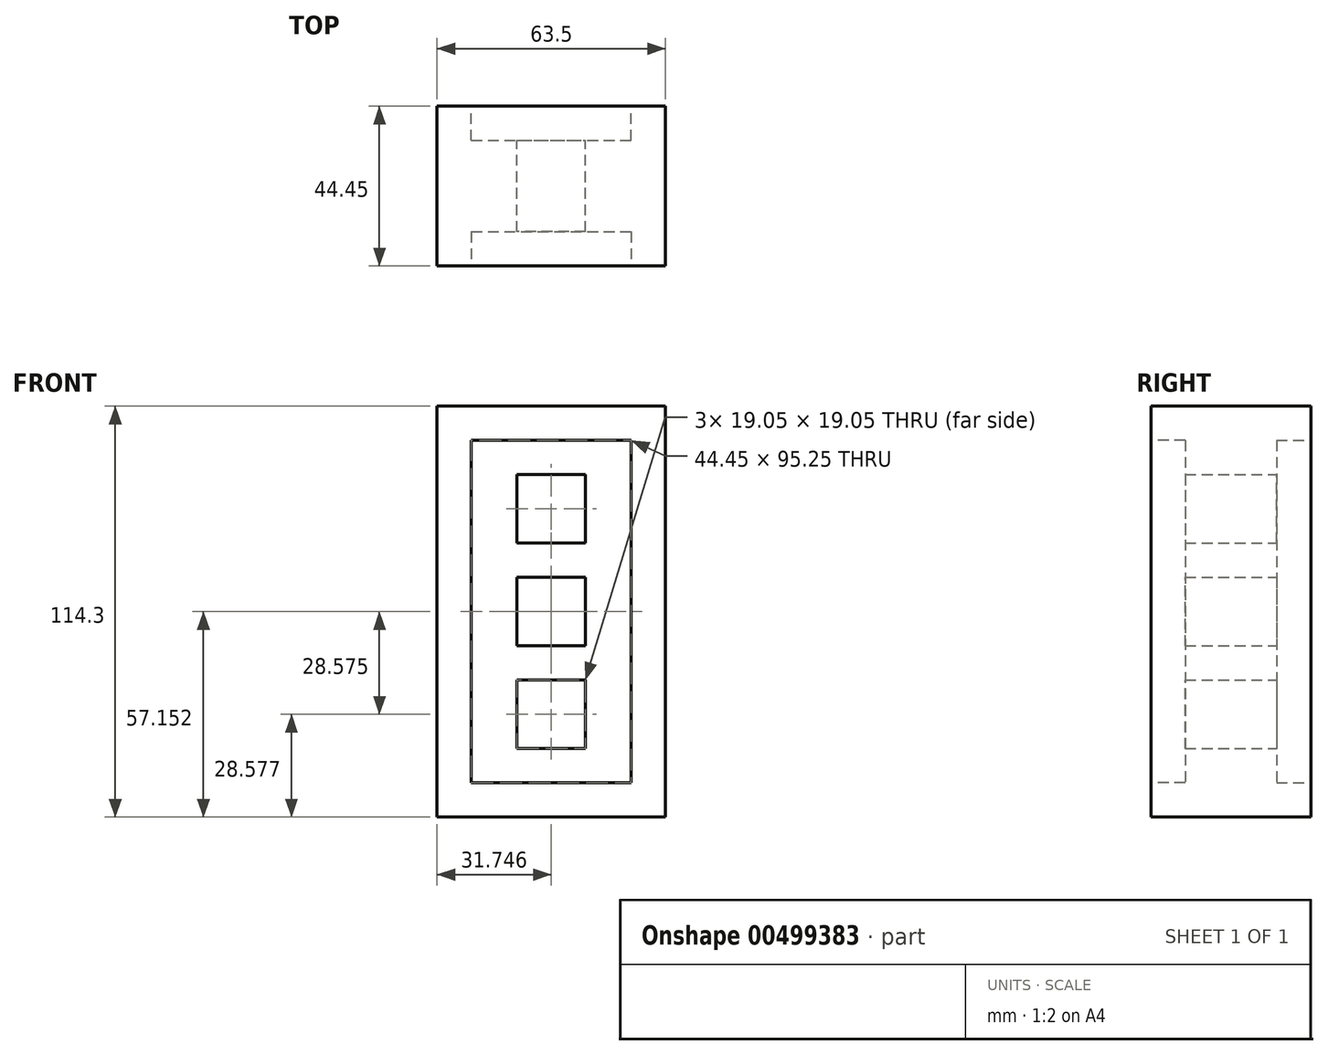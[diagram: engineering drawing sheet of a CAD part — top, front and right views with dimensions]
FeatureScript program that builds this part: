
annotation { "Feature Type Name" : "Feature", "Feature Type Description" : "" }
export const myFeature = defineFeature(function(context is Context, id is Id, definition is map)
    precondition{}
    {
        {
            var Q0;
            Q0=qCreatedBy(makeId("Front.planeOp"),FACE);
            var sketch = newSketch(context, id + "F0", { "sketchPlane" : qUnion([Q0])});
            skLineSegment(sketch, "E0.bottom", {"start": v(-7.78, 6.67) * mm, "end": v(11.27, 6.67) * mm});
            skLineSegment(sketch, "E0.top", {"start": v(-7.78, -12.38) * mm, "end": v(11.27, -12.38) * mm});
            skLineSegment(sketch, "E0.left", {"start": v(-7.78, 6.67) * mm, "end": v(-7.78, -12.38) * mm});
            skLineSegment(sketch, "E0.right", {"start": v(11.27, 6.67) * mm, "end": v(11.27, -12.38) * mm});
            skLineSegment(sketch, "E1.bottom", {"start": v(-7.78, 16.2) * mm, "end": v(11.27, 16.2) * mm});
            skLineSegment(sketch, "E1.top", {"start": v(-7.78, 35.24) * mm, "end": v(11.27, 35.24) * mm});
            skLineSegment(sketch, "E1.left", {"start": v(-7.78, 16.2) * mm, "end": v(-7.78, 35.24) * mm});
            skLineSegment(sketch, "E1.right", {"start": v(11.27, 16.2) * mm, "end": v(11.27, 35.24) * mm});
            skLineSegment(sketch, "E2.bottom", {"start": v(-7.78, -21.9) * mm, "end": v(11.27, -21.9) * mm});
            skLineSegment(sketch, "E2.top", {"start": v(-7.78, -40.96) * mm, "end": v(11.27, -40.96) * mm});
            skLineSegment(sketch, "E2.left", {"start": v(-7.78, -21.9) * mm, "end": v(-7.78, -40.96) * mm});
            skLineSegment(sketch, "E2.right", {"start": v(11.27, -21.9) * mm, "end": v(11.27, -40.96) * mm});
            skLineSegment(sketch, "E3.bottom", {"start": v(-20.48, 44.77) * mm, "end": v(23.97, 44.77) * mm});
            skLineSegment(sketch, "E3.top", {"start": v(-20.48, -50.48) * mm, "end": v(23.97, -50.48) * mm});
            skLineSegment(sketch, "E3.left", {"start": v(-20.48, 44.77) * mm, "end": v(-20.48, -50.48) * mm});
            skLineSegment(sketch, "E3.right", {"start": v(23.97, 44.77) * mm, "end": v(23.97, -50.48) * mm});
            skLineSegment(sketch, "E4.bottom", {"start": v(-30, 54.3) * mm, "end": v(33.5, 54.3) * mm});
            skLineSegment(sketch, "E4.top", {"start": v(-30, -60) * mm, "end": v(33.5, -60) * mm});
            skLineSegment(sketch, "E4.left", {"start": v(-30, 54.3) * mm, "end": v(-30, -60) * mm});
            skLineSegment(sketch, "E4.right", {"start": v(33.5, 54.3) * mm, "end": v(33.5, -60) * mm});
            skSolve(sketch);
        }
        {
            var Q0;
            Q0=makeQuery(id+"F0.imprint","IMPRINT",FACE,{"disambiguationData":[TD([[makeQuery(id+"F0.imprint","IMPRINT",EDGE,{"derivedFrom":sQuery(id+"F0.wireOp",EDGE,"E0.bottom")}),1.0]])]});
            var Q1;
            Q1=makeQuery(id+"F0.imprint","IMPRINT",FACE,{"disambiguationData":[TD([[makeQuery(id+"F0.imprint","IMPRINT",EDGE,{"derivedFrom":sQuery(id+"F0.wireOp",EDGE,"E3.bottom")}),1.0]])]});
            var Q2;
            Q2=makeQuery(id+"F0.imprint","IMPRINT",FACE,{"disambiguationData":[TD([[makeQuery(id+"F0.imprint","IMPRINT",EDGE,{"derivedFrom":sQuery(id+"F0.wireOp",EDGE,"E2.bottom")}),-1.0]])]});
            var Q3;
            Q3=makeQuery(id+"F0.imprint","IMPRINT",FACE,{"disambiguationData":[TD([[makeQuery(id+"F0.imprint","IMPRINT",EDGE,{"derivedFrom":sQuery(id+"F0.wireOp",EDGE,"E1.bottom")}),1.0]])]});
            var Q4;
            Q4=makeQuery(id+"F0.imprint","IMPRINT",FACE,{"disambiguationData":[TD([[makeQuery(id+"F0.imprint","IMPRINT",EDGE,{"derivedFrom":sQuery(id+"F0.wireOp",EDGE,"E0.bottom")}),-1.0]])]});
            extrude(context, id + "F1", {"entities" : qUnion([Q0, Q1, Q2, Q3, Q4]), "depth" : 44.45 * mm});
        }
        {
            var Q0;
            Q0=makeQuery(id+"F0.imprint","IMPRINT",FACE,{"disambiguationData":[TD([[makeQuery(id+"F0.imprint","IMPRINT",EDGE,{"derivedFrom":sQuery(id+"F0.wireOp",EDGE,"E1.bottom")}),1.0]])]});
            var Q1;
            Q1=makeQuery(id+"F0.imprint","IMPRINT",FACE,{"disambiguationData":[TD([[makeQuery(id+"F0.imprint","IMPRINT",EDGE,{"derivedFrom":sQuery(id+"F0.wireOp",EDGE,"E0.bottom")}),-1.0]])]});
            var Q2;
            Q2=makeQuery(id+"F0.imprint","IMPRINT",FACE,{"disambiguationData":[TD([[makeQuery(id+"F0.imprint","IMPRINT",EDGE,{"derivedFrom":sQuery(id+"F0.wireOp",EDGE,"E2.bottom")}),-1.0]])]});
            extrude(context, id + "F2", {"entities" : qUnion([Q0, Q1, Q2]), "operationType" : NewBodyOperationType.REMOVE, "endBound" : BoundingType.THROUGH_ALL, "depth" : 25.4 * mm});
        }
        {
            var Q0;
            Q0=makeQuery(id+"F0.imprint","IMPRINT",FACE,{"disambiguationData":[TD([[makeQuery(id+"F0.imprint","IMPRINT",EDGE,{"derivedFrom":sQuery(id+"F0.wireOp",EDGE,"E0.bottom")}),1.0]])]});
            extrude(context, id + "F3", {"entities" : qUnion([Q0]), "operationType" : NewBodyOperationType.REMOVE, "depth" : 9.52 * mm});
        }
        {
            var Q0;
            Q0=makeQuery(id+"F1.opExtrude","CAP_FACE",FACE,{"disambiguationData":[OSD([sQuery(id+"F0.wireOp",EDGE,"E4.bottom"),sQuery(id+"F0.wireOp",EDGE,"E4.top"),sQuery(id+"F0.wireOp",EDGE,"E4.left"),sQuery(id+"F0.wireOp",EDGE,"E4.right")])],"isStart":false});
            var sketch = newSketch(context, id + "F4", { "sketchPlane" : qUnion([Q0])});
            skLineSegment(sketch, "E5.bottom", {"start": v(-20.48, 44.77) * mm, "end": v(23.97, 44.77) * mm});
            skLineSegment(sketch, "E5.top", {"start": v(-20.48, -50.48) * mm, "end": v(23.97, -50.48) * mm});
            skLineSegment(sketch, "E5.left", {"start": v(-20.48, 44.77) * mm, "end": v(-20.48, -50.48) * mm});
            skLineSegment(sketch, "E5.right", {"start": v(23.97, 44.77) * mm, "end": v(23.97, -50.48) * mm});
            skSolve(sketch);
        }
        {
            var Q0;
            Q0=makeQuery(id+"F4.imprint","IMPRINT",FACE,{"disambiguationData":[TD([[makeQuery(id+"F4.imprint","IMPRINT",EDGE,{"derivedFrom":sQuery(id+"F4.wireOp",EDGE,"E5.bottom")}),-1.0]])]});
            extrude(context, id + "F5", {"entities" : qUnion([Q0]), "operationType" : NewBodyOperationType.REMOVE, "oppositeDirection" : true, "depth" : 9.52 * mm});
        }
    });
